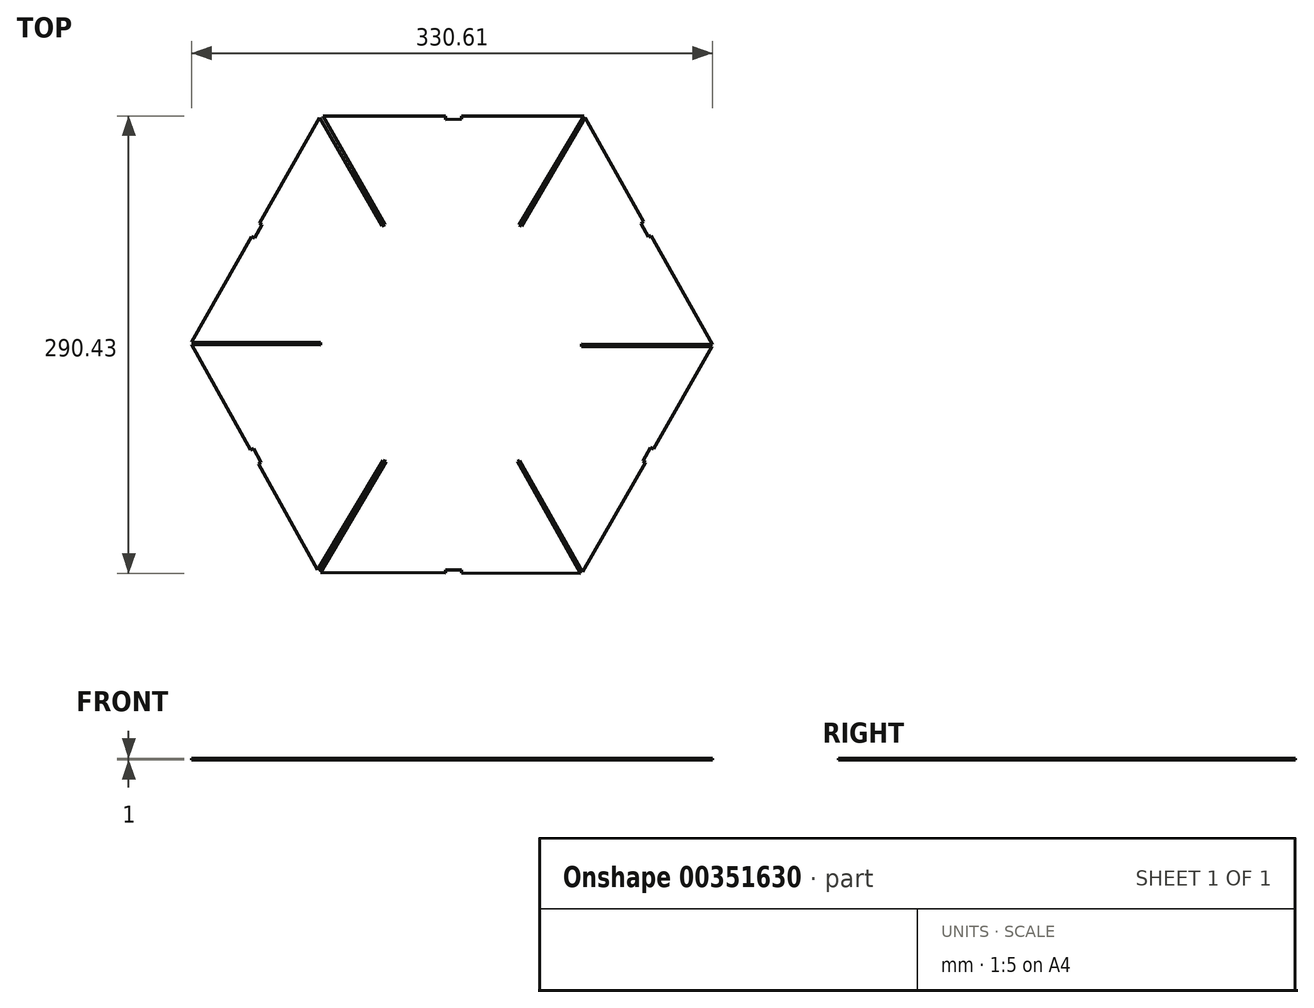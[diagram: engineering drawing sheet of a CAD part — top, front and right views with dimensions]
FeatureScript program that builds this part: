
annotation { "Feature Type Name" : "Feature", "Feature Type Description" : "" }
export const myFeature = defineFeature(function(context is Context, id is Id, definition is map)
    precondition{}
    {
        {
            var Q0;
            Q0=qCreatedBy(makeId("Top.planeOp"),FACE);
            var sketch = newSketch(context, id + "F0", { "sketchPlane" : qUnion([Q0])});
            skLineSegment(sketch, "E0", {"start": v(-250.35, 294.47) * mm, "end": v(-211.1, 225.62) * mm});
            skLineSegment(sketch, "E1", {"start": v(-212.85, 224.65) * mm, "end": v(-252.72, 293.8) * mm});
            skLineSegment(sketch, "E2", {"start": v(-84, 293.57) * mm, "end": v(-124.43, 224.66) * mm});
            skLineSegment(sketch, "E3", {"start": v(-86.95, 4.21) * mm, "end": v(-126.77, 75.2) * mm});
            skLineSegment(sketch, "E4", {"start": v(-126.77, 75.2) * mm, "end": v(-125.57, 76.02) * mm});
            skLineSegment(sketch, "E5", {"start": v(-125.57, 76.02) * mm, "end": v(-85.54, 4.92) * mm});
            skLineSegment(sketch, "E6", {"start": v(-254.03, 6.48) * mm, "end": v(-212.25, 75.92) * mm});
            skLineSegment(sketch, "E7", {"start": v(-252.1, 4.6) * mm, "end": v(-210.48, 75.12) * mm});
            skLineSegment(sketch, "E8", {"start": v(-333.76, 150.95) * mm, "end": v(-252.72, 293.8) * mm});
            skLineSegment(sketch, "E9", {"start": v(-333.76, 149.56) * mm, "end": v(-254.03, 6.48) * mm});
            skLineSegment(sketch, "E10", {"start": v(-252.1, 4.6) * mm, "end": v(-86.95, 4.21) * mm});
            skLineSegment(sketch, "E11", {"start": v(-250.35, 294.47) * mm, "end": v(-84.74, 294.64) * mm});
            skLineSegment(sketch, "E12", {"start": v(-84, 293.57) * mm, "end": v(-3.15, 149.65) * mm});
            skLineSegment(sketch, "E13", {"start": v(112.8, 289.57) * mm, "end": v(239.42, 289.57) * mm});
            skLineSegment(sketch, "E14", {"start": v(240.63, 288.54) * mm, "end": v(303, 178.67) * mm});
            skLineSegment(sketch, "E15", {"start": v(302.98, 177.38) * mm, "end": v(240.54, 67.56) * mm});
            skLineSegment(sketch, "E16", {"start": v(111.35, 67.6) * mm, "end": v(239.28, 67.23) * mm});
            skLineSegment(sketch, "E17", {"start": v(47.38, 177.39) * mm, "end": v(109.98, 67.78) * mm});
            skLineSegment(sketch, "E18", {"start": v(47.44, 178.96) * mm, "end": v(111.62, 289.24) * mm});
            skLineSegment(sketch, "E19", {"start": v(12.87, -130.32) * mm, "end": v(12.87, -166.75) * mm});
            skLineSegment(sketch, "E20", {"start": v(12.87, -166.75) * mm, "end": v(92.46, -167.04) * mm});
            skLineSegment(sketch, "E21", {"start": v(92.46, -167.04) * mm, "end": v(92.46, -168.32) * mm});
            skLineSegment(sketch, "E22", {"start": v(92.46, -168.32) * mm, "end": v(13.17, -168.32) * mm});
            skLineSegment(sketch, "E23", {"start": v(13.17, -168.32) * mm, "end": v(12.87, -198.92) * mm});
            skLineSegment(sketch, "E24", {"start": v(12.87, -198.92) * mm, "end": v(13.17, -205.1) * mm});
            skLineSegment(sketch, "E25", {"start": v(13.17, -205.1) * mm, "end": v(12.87, -235.71) * mm});
            skLineSegment(sketch, "E26", {"start": v(12.87, -235.71) * mm, "end": v(73.4, -236) * mm});
            skLineSegment(sketch, "E27", {"start": v(73.4, -236) * mm, "end": v(73.4, -237.3) * mm});
            skLineSegment(sketch, "E28", {"start": v(73.4, -237.3) * mm, "end": v(13.17, -237.3) * mm});
            skLineSegment(sketch, "E29", {"start": v(13.17, -237.3) * mm, "end": v(12.87, -270.02) * mm});
            skLineSegment(sketch, "E30", {"start": v(12.87, -270.02) * mm, "end": v(49.25, -270.3) * mm});
            skLineSegment(sketch, "E31", {"start": v(49.25, -270.3) * mm, "end": v(49.25, -271.6) * mm});
            skLineSegment(sketch, "E32", {"start": v(49.25, -271.6) * mm, "end": v(13.17, -271.6) * mm});
            skLineSegment(sketch, "E33", {"start": v(13.17, -271.6) * mm, "end": v(12.87, -287.73) * mm});
            skLineSegment(sketch, "E34", {"start": v(12.87, -287.73) * mm, "end": v(21.59, -287.39) * mm});
            skLineSegment(sketch, "E35", {"start": v(21.59, -287.39) * mm, "end": v(35.18, -285.85) * mm});
            skLineSegment(sketch, "E36", {"start": v(35.18, -285.85) * mm, "end": v(48.35, -283.43) * mm});
            skLineSegment(sketch, "E37", {"start": v(48.35, -283.43) * mm, "end": v(60.91, -280.2) * mm});
            skLineSegment(sketch, "E38", {"start": v(60.91, -280.2) * mm, "end": v(72.63, -276.27) * mm});
            skLineSegment(sketch, "E39", {"start": v(72.63, -276.27) * mm, "end": v(83.5, -271.8) * mm});
            skLineSegment(sketch, "E40", {"start": v(83.5, -271.8) * mm, "end": v(93.48, -266.93) * mm});
            skLineSegment(sketch, "E41", {"start": v(12.87, -96) * mm, "end": v(12.87, -130.32) * mm});
            skLineSegment(sketch, "E42", {"start": v(13.17, -66.1) * mm, "end": v(12.87, -96.01) * mm});
            skLineSegment(sketch, "E43", {"start": v(12.87, -27.4) * mm, "end": v(12.87, -63.82) * mm});
            skLineSegment(sketch, "E44", {"start": v(12.87, -63.82) * mm, "end": v(92.46, -64.1) * mm});
            skLineSegment(sketch, "E45", {"start": v(93.48, 34.15) * mm, "end": v(83.5, 39.02) * mm});
            skLineSegment(sketch, "E46", {"start": v(83.5, 39.02) * mm, "end": v(72.63, 43.5) * mm});
            skLineSegment(sketch, "E47", {"start": v(72.63, 43.5) * mm, "end": v(60.91, 47.42) * mm});
            skLineSegment(sketch, "E48", {"start": v(60.91, 47.42) * mm, "end": v(48.35, 50.64) * mm});
            skLineSegment(sketch, "E49", {"start": v(48.35, 50.64) * mm, "end": v(35.17, 53.07) * mm});
            skLineSegment(sketch, "E50", {"start": v(35.17, 53.07) * mm, "end": v(21.59, 54.6) * mm});
            skLineSegment(sketch, "E51", {"start": v(21.59, 54.6) * mm, "end": v(12.87, 54.95) * mm});
            skLineSegment(sketch, "E52", {"start": v(12.87, 54.95) * mm, "end": v(12.87, 38.75) * mm});
            skLineSegment(sketch, "E53", {"start": v(12.87, 38.75) * mm, "end": v(49.25, 38.47) * mm});
            skLineSegment(sketch, "E54", {"start": v(49.25, 38.47) * mm, "end": v(49.25, 37.17) * mm});
            skLineSegment(sketch, "E55", {"start": v(49.25, 37.17) * mm, "end": v(13.17, 37.17) * mm});
            skLineSegment(sketch, "E56", {"start": v(13.17, 37.17) * mm, "end": v(12.87, 5.16) * mm});
            skLineSegment(sketch, "E57", {"start": v(12.87, 5.16) * mm, "end": v(73.39, 4.86) * mm});
            skLineSegment(sketch, "E58", {"start": v(73.39, 4.86) * mm, "end": v(73.39, 3.22) * mm});
            skLineSegment(sketch, "E59", {"start": v(73.39, 3.22) * mm, "end": v(13.17, 3.22) * mm});
            skLineSegment(sketch, "E60", {"start": v(13.17, 3.22) * mm, "end": v(12.87, -27.4) * mm});
            skLineSegment(sketch, "E61", {"start": v(92.1, -168.46) * mm, "end": v(12.87, -168.45) * mm});
            skLineSegment(sketch, "E62", {"start": v(12.87, -168.45) * mm, "end": v(12.87, -166.95) * mm});
            skLineSegment(sketch, "E63", {"start": v(12.87, -166.95) * mm, "end": v(92.1, -166.96) * mm});
            skLineSegment(sketch, "E64", {"start": v(92.1, -166.96) * mm, "end": v(92.1, -168.46) * mm});
            skLineSegment(sketch, "E65", {"start": v(171.06, -171.15) * mm, "end": v(93.48, -266.93) * mm});
            skLineSegment(sketch, "E66", {"start": v(93.48, 34.15) * mm, "end": v(171.18, -62) * mm});
            skLineSegment(sketch, "E67", {"start": v(171.18, -62) * mm, "end": v(171.06, -171.15) * mm});
            skLineSegment(sketch, "E68", {"start": v(92.24, -65.74) * mm, "end": v(13.02, -65.73) * mm});
            skLineSegment(sketch, "E69", {"start": v(13.02, -65.73) * mm, "end": v(13.02, -64.23) * mm});
            skLineSegment(sketch, "E70", {"start": v(13.02, -64.23) * mm, "end": v(92.24, -64.24) * mm});
            skLineSegment(sketch, "E71", {"start": v(92.24, -64.24) * mm, "end": v(92.24, -65.74) * mm});
            skLineSegment(sketch, "E72", {"start": v(12.87, -66) * mm, "end": v(92.46, -66) * mm});
            skLineSegment(sketch, "E73", {"start": v(73.01, 3.26) * mm, "end": v(13.02, 3.27) * mm});
            skLineSegment(sketch, "E74", {"start": v(13.02, 3.27) * mm, "end": v(13.02, 4.77) * mm});
            skLineSegment(sketch, "E75", {"start": v(13.02, 4.77) * mm, "end": v(73.01, 4.76) * mm});
            skLineSegment(sketch, "E76", {"start": v(73.01, 4.76) * mm, "end": v(73.01, 3.26) * mm});
            skLineSegment(sketch, "E77", {"start": v(73.42, -237.43) * mm, "end": v(12.87, -237.42) * mm});
            skLineSegment(sketch, "E78", {"start": v(12.87, -237.42) * mm, "end": v(12.87, -235.92) * mm});
            skLineSegment(sketch, "E79", {"start": v(12.87, -235.92) * mm, "end": v(73.42, -235.93) * mm});
            skLineSegment(sketch, "E80", {"start": v(73.42, -235.93) * mm, "end": v(73.42, -237.43) * mm});
            skLineSegment(sketch, "E81", {"start": v(48.74, -271.47) * mm, "end": v(12.87, -271.46) * mm});
            skLineSegment(sketch, "E82", {"start": v(12.87, -271.46) * mm, "end": v(12.87, -269.96) * mm});
            skLineSegment(sketch, "E83", {"start": v(12.87, -269.96) * mm, "end": v(48.74, -269.97) * mm});
            skLineSegment(sketch, "E84", {"start": v(48.74, -269.97) * mm, "end": v(48.74, -271.47) * mm});
            skLineSegment(sketch, "E85", {"start": v(49.27, 37.27) * mm, "end": v(12.88, 37.28) * mm});
            skLineSegment(sketch, "E86", {"start": v(12.88, 37.28) * mm, "end": v(12.88, 38.78) * mm});
            skLineSegment(sketch, "E87", {"start": v(12.88, 38.78) * mm, "end": v(49.27, 38.77) * mm});
            skLineSegment(sketch, "E88", {"start": v(49.27, 38.77) * mm, "end": v(49.27, 37.27) * mm});
            skLineSegment(sketch, "E89", {"start": v(176.64, -137.23) * mm, "end": v(176.64, -173.66) * mm});
            skLineSegment(sketch, "E90", {"start": v(176.64, -173.66) * mm, "end": v(256.22, -173.94) * mm});
            skLineSegment(sketch, "E91", {"start": v(256.22, -173.94) * mm, "end": v(256.22, -175.22) * mm});
            skLineSegment(sketch, "E92", {"start": v(256.22, -175.22) * mm, "end": v(176.94, -175.22) * mm});
            skLineSegment(sketch, "E93", {"start": v(176.94, -175.22) * mm, "end": v(176.64, -205.83) * mm});
            skLineSegment(sketch, "E94", {"start": v(176.64, -205.83) * mm, "end": v(176.94, -212) * mm});
            skLineSegment(sketch, "E95", {"start": v(176.94, -212) * mm, "end": v(176.64, -242.62) * mm});
            skLineSegment(sketch, "E96", {"start": v(176.64, -242.62) * mm, "end": v(237.16, -242.91) * mm});
            skLineSegment(sketch, "E97", {"start": v(237.16, -242.91) * mm, "end": v(237.16, -244.2) * mm});
            skLineSegment(sketch, "E98", {"start": v(237.16, -244.2) * mm, "end": v(176.94, -244.2) * mm});
            skLineSegment(sketch, "E99", {"start": v(176.94, -244.2) * mm, "end": v(176.64, -276.93) * mm});
            skLineSegment(sketch, "E100", {"start": v(176.64, -276.93) * mm, "end": v(213, -277.22) * mm});
            skLineSegment(sketch, "E101", {"start": v(213, -277.22) * mm, "end": v(213, -278.5) * mm});
            skLineSegment(sketch, "E102", {"start": v(213, -278.5) * mm, "end": v(176.94, -278.5) * mm});
            skLineSegment(sketch, "E103", {"start": v(176.94, -278.5) * mm, "end": v(176.64, -294.64) * mm});
            skLineSegment(sketch, "E104", {"start": v(176.64, -294.64) * mm, "end": v(185.35, -294.3) * mm});
            skLineSegment(sketch, "E105", {"start": v(185.35, -294.3) * mm, "end": v(198.95, -292.76) * mm});
            skLineSegment(sketch, "E106", {"start": v(198.95, -292.76) * mm, "end": v(212.12, -290.34) * mm});
            skLineSegment(sketch, "E107", {"start": v(212.12, -290.34) * mm, "end": v(224.68, -287.1) * mm});
            skLineSegment(sketch, "E108", {"start": v(224.68, -287.1) * mm, "end": v(236.4, -283.18) * mm});
            skLineSegment(sketch, "E109", {"start": v(236.4, -283.18) * mm, "end": v(247.26, -278.72) * mm});
            skLineSegment(sketch, "E110", {"start": v(247.26, -278.72) * mm, "end": v(257.25, -273.84) * mm});
            skLineSegment(sketch, "E111", {"start": v(176.64, -102.91) * mm, "end": v(176.64, -137.23) * mm});
            skLineSegment(sketch, "E112", {"start": v(176.94, -73.02) * mm, "end": v(176.64, -102.92) * mm});
            skLineSegment(sketch, "E113", {"start": v(176.64, -34.3) * mm, "end": v(176.64, -70.73) * mm});
            skLineSegment(sketch, "E114", {"start": v(176.64, -70.73) * mm, "end": v(256.22, -71.02) * mm});
            skLineSegment(sketch, "E115", {"start": v(257.25, 27.24) * mm, "end": v(247.26, 32.11) * mm});
            skLineSegment(sketch, "E116", {"start": v(247.26, 32.11) * mm, "end": v(236.4, 36.6) * mm});
            skLineSegment(sketch, "E117", {"start": v(236.4, 36.6) * mm, "end": v(224.68, 40.51) * mm});
            skLineSegment(sketch, "E118", {"start": v(224.68, 40.51) * mm, "end": v(212.12, 43.73) * mm});
            skLineSegment(sketch, "E119", {"start": v(212.12, 43.73) * mm, "end": v(198.94, 46.16) * mm});
            skLineSegment(sketch, "E120", {"start": v(198.94, 46.16) * mm, "end": v(185.35, 47.7) * mm});
            skLineSegment(sketch, "E121", {"start": v(185.35, 47.7) * mm, "end": v(176.64, 48.04) * mm});
            skLineSegment(sketch, "E122", {"start": v(176.64, 48.04) * mm, "end": v(176.64, 31.84) * mm});
            skLineSegment(sketch, "E123", {"start": v(176.64, 31.84) * mm, "end": v(213, 31.56) * mm});
            skLineSegment(sketch, "E124", {"start": v(213, 31.56) * mm, "end": v(213, 30.27) * mm});
            skLineSegment(sketch, "E125", {"start": v(213, 30.27) * mm, "end": v(176.94, 30.27) * mm});
            skLineSegment(sketch, "E126", {"start": v(176.94, 30.27) * mm, "end": v(176.64, -1.75) * mm});
            skLineSegment(sketch, "E127", {"start": v(176.64, -1.75) * mm, "end": v(237.15, -2.05) * mm});
            skLineSegment(sketch, "E128", {"start": v(237.15, -2.05) * mm, "end": v(237.15, -3.69) * mm});
            skLineSegment(sketch, "E129", {"start": v(237.15, -3.69) * mm, "end": v(176.94, -3.69) * mm});
            skLineSegment(sketch, "E130", {"start": v(176.94, -3.69) * mm, "end": v(176.64, -34.3) * mm});
            skLineSegment(sketch, "E131", {"start": v(255.85, -175.37) * mm, "end": v(176.64, -175.36) * mm});
            skLineSegment(sketch, "E132", {"start": v(176.64, -175.36) * mm, "end": v(176.64, -173.86) * mm});
            skLineSegment(sketch, "E133", {"start": v(176.64, -173.86) * mm, "end": v(255.85, -173.87) * mm});
            skLineSegment(sketch, "E134", {"start": v(255.85, -173.87) * mm, "end": v(255.85, -175.37) * mm});
            skLineSegment(sketch, "E135", {"start": v(334.82, -178.06) * mm, "end": v(257.25, -273.84) * mm});
            skLineSegment(sketch, "E136", {"start": v(257.25, 27.24) * mm, "end": v(334.94, -68.92) * mm});
            skLineSegment(sketch, "E137", {"start": v(334.94, -68.92) * mm, "end": v(334.82, -178.06) * mm});
            skLineSegment(sketch, "E138", {"start": v(256, -72.65) * mm, "end": v(176.79, -72.63) * mm});
            skLineSegment(sketch, "E139", {"start": v(176.79, -72.63) * mm, "end": v(176.79, -71.13) * mm});
            skLineSegment(sketch, "E140", {"start": v(176.79, -71.13) * mm, "end": v(256, -71.15) * mm});
            skLineSegment(sketch, "E141", {"start": v(256, -71.15) * mm, "end": v(256, -72.65) * mm});
            skLineSegment(sketch, "E142", {"start": v(176.64, -72.91) * mm, "end": v(256.22, -72.91) * mm});
            skLineSegment(sketch, "E143", {"start": v(236.78, -3.65) * mm, "end": v(176.79, -3.64) * mm});
            skLineSegment(sketch, "E144", {"start": v(176.79, -3.64) * mm, "end": v(176.79, -2.14) * mm});
            skLineSegment(sketch, "E145", {"start": v(176.79, -2.14) * mm, "end": v(236.78, -2.15) * mm});
            skLineSegment(sketch, "E146", {"start": v(236.78, -2.15) * mm, "end": v(236.78, -3.65) * mm});
            skLineSegment(sketch, "E147", {"start": v(237.19, -244.34) * mm, "end": v(176.64, -244.32) * mm});
            skLineSegment(sketch, "E148", {"start": v(176.64, -244.32) * mm, "end": v(176.64, -242.82) * mm});
            skLineSegment(sketch, "E149", {"start": v(176.64, -242.82) * mm, "end": v(237.19, -242.84) * mm});
            skLineSegment(sketch, "E150", {"start": v(237.19, -242.84) * mm, "end": v(237.19, -244.34) * mm});
            skLineSegment(sketch, "E151", {"start": v(212.5, -278.38) * mm, "end": v(176.64, -278.37) * mm});
            skLineSegment(sketch, "E152", {"start": v(176.64, -278.37) * mm, "end": v(176.64, -276.87) * mm});
            skLineSegment(sketch, "E153", {"start": v(176.64, -276.87) * mm, "end": v(212.5, -276.88) * mm});
            skLineSegment(sketch, "E154", {"start": v(212.5, -276.88) * mm, "end": v(212.5, -278.38) * mm});
            skLineSegment(sketch, "E155", {"start": v(213.04, 30.36) * mm, "end": v(176.65, 30.37) * mm});
            skLineSegment(sketch, "E156", {"start": v(176.65, 30.37) * mm, "end": v(176.65, 31.87) * mm});
            skLineSegment(sketch, "E157", {"start": v(176.65, 31.87) * mm, "end": v(213.04, 31.86) * mm});
            skLineSegment(sketch, "E158", {"start": v(213.04, 31.86) * mm, "end": v(213.04, 30.36) * mm});
            skLineSegment(sketch, "E159", {"start": v(-84.74, 294.64) * mm, "end": v(-125.8, 225.5) * mm});
            skLineSegment(sketch, "E160", {"start": v(-251.86, 149.23) * mm, "end": v(-333.76, 149.56) * mm});
            skLineSegment(sketch, "E161", {"start": v(-333.76, 150.96) * mm, "end": v(-333.76, 150.96) * mm});
            skLineSegment(sketch, "E162", {"start": v(-333.76, 150.96) * mm, "end": v(-251.85, 150.64) * mm});
            skLineSegment(sketch, "E163", {"start": v(-86.22, 149.98) * mm, "end": v(-3.15, 149.65) * mm});
            skLineSegment(sketch, "E164", {"start": v(-3.32, 148.25) * mm, "end": v(-86.27, 148.22) * mm});
            skLineSegment(sketch, "E165", {"start": v(47.87, 179.02) * mm, "end": v(109.23, 178.78) * mm});
            skLineSegment(sketch, "E166", {"start": v(109.23, 178.78) * mm, "end": v(109.22, 177.38) * mm});
            skLineSegment(sketch, "E167", {"start": v(109.22, 177.38) * mm, "end": v(47.35, 177.62) * mm});
            skLineSegment(sketch, "E168", {"start": v(241.63, 179.02) * mm, "end": v(302.98, 178.78) * mm});
            skLineSegment(sketch, "E169", {"start": v(302.98, 178.78) * mm, "end": v(302.98, 177.38) * mm});
            skLineSegment(sketch, "E170", {"start": v(302.98, 177.38) * mm, "end": v(241.63, 177.62) * mm});
            skLineSegment(sketch, "E171", {"start": v(-251.85, 150.64) * mm, "end": v(-251.86, 149.23) * mm});
            skLineSegment(sketch, "E172", {"start": v(-86.22, 149.98) * mm, "end": v(-86.27, 148.22) * mm});
            skLineSegment(sketch, "E173", {"start": v(-248.6, -2.14) * mm, "end": v(-252.57, -2.14) * mm});
            skLineSegment(sketch, "E174", {"start": v(-252.57, -2.14) * mm, "end": v(-212.18, -72.78) * mm});
            skLineSegment(sketch, "E175", {"start": v(-212.18, -72.78) * mm, "end": v(-213.4, -73.24) * mm});
            skLineSegment(sketch, "E176", {"start": v(-213.4, -73.24) * mm, "end": v(-253.9, -2.98) * mm});
            skLineSegment(sketch, "E177", {"start": v(-85.17, -3.2) * mm, "end": v(-126.38, -73.58) * mm});
            skLineSegment(sketch, "E178", {"start": v(-126.38, -73.58) * mm, "end": v(-127.79, -72.55) * mm});
            skLineSegment(sketch, "E179", {"start": v(-88.13, -292.57) * mm, "end": v(-127.95, -221.58) * mm});
            skLineSegment(sketch, "E180", {"start": v(-127.95, -221.58) * mm, "end": v(-126.75, -220.77) * mm});
            skLineSegment(sketch, "E181", {"start": v(-126.75, -220.77) * mm, "end": v(-86.72, -291.87) * mm});
            skLineSegment(sketch, "E182", {"start": v(-254.23, -290.57) * mm, "end": v(-213.04, -220.78) * mm});
            skLineSegment(sketch, "E183", {"start": v(-213.04, -220.78) * mm, "end": v(-211.67, -221.79) * mm});
            skLineSegment(sketch, "E184", {"start": v(-253.27, -292.2) * mm, "end": v(-211.67, -221.66) * mm});
            skLineSegment(sketch, "E185", {"start": v(-334.94, -145.83) * mm, "end": v(-253.9, -2.98) * mm});
            skLineSegment(sketch, "E186", {"start": v(-334.94, -147.23) * mm, "end": v(-254.23, -290.57) * mm});
            skLineSegment(sketch, "E187", {"start": v(-253.27, -292.2) * mm, "end": v(-88.36, -292.54) * mm});
            skLineSegment(sketch, "E188", {"start": v(-86.72, -291.87) * mm, "end": v(-4.33, -148.76) * mm});
            skLineSegment(sketch, "E189", {"start": v(-249.9, -2.14) * mm, "end": v(-85.92, -2.14) * mm});
            skLineSegment(sketch, "E190", {"start": v(-85.17, -3.2) * mm, "end": v(-4.33, -147.26) * mm});
            skLineSegment(sketch, "E191", {"start": v(-213.34, -73.46) * mm, "end": v(-214.08, -72.16) * mm});
            skLineSegment(sketch, "E192", {"start": v(-214.08, -72.16) * mm, "end": v(-212.77, -71.42) * mm});
            skLineSegment(sketch, "E193", {"start": v(-212.77, -71.42) * mm, "end": v(-212.03, -72.73) * mm});
            skLineSegment(sketch, "E194", {"start": v(-212.03, -72.73) * mm, "end": v(-213.34, -73.46) * mm});
            skLineSegment(sketch, "E195", {"start": v(-126.52, -73.36) * mm, "end": v(-127.79, -72.55) * mm});
            skLineSegment(sketch, "E196", {"start": v(-127.79, -72.55) * mm, "end": v(-126.98, -71.29) * mm});
            skLineSegment(sketch, "E197", {"start": v(-126.98, -71.29) * mm, "end": v(-125.71, -72.1) * mm});
            skLineSegment(sketch, "E198", {"start": v(-125.71, -72.1) * mm, "end": v(-126.52, -73.36) * mm});
            skLineSegment(sketch, "E199", {"start": v(-85.92, -2.14) * mm, "end": v(-127.79, -72.55) * mm});
            skLineSegment(sketch, "E200", {"start": v(-253.04, -147.55) * mm, "end": v(-334.94, -147.23) * mm});
            skLineSegment(sketch, "E201", {"start": v(-334.94, -147.23) * mm, "end": v(-334.94, -145.82) * mm});
            skLineSegment(sketch, "E202", {"start": v(-334.94, -145.82) * mm, "end": v(-253.04, -146.15) * mm});
            skLineSegment(sketch, "E203", {"start": v(-87.23, -146.8) * mm, "end": v(-4.33, -147.13) * mm});
            skLineSegment(sketch, "E204", {"start": v(-4.33, -147.13) * mm, "end": v(-4.33, -148.53) * mm});
            skLineSegment(sketch, "E205", {"start": v(-4.33, -148.53) * mm, "end": v(-87.47, -148.2) * mm});
            skLineSegment(sketch, "E206", {"start": v(-253.04, -146.15) * mm, "end": v(-253.04, -147.55) * mm});
            skLineSegment(sketch, "E207", {"start": v(-87.23, -146.8) * mm, "end": v(-87.47, -148.2) * mm});
            skLineSegment(sketch, "E208", {"start": v(241.63, 179.02) * mm, "end": v(241.63, 177.62) * mm});
            skLineSegment(sketch, "E209", {"start": v(208.5, 236.25) * mm, "end": v(239.42, 289.24) * mm});
            skLineSegment(sketch, "E210", {"start": v(239.42, 289.24) * mm, "end": v(240.63, 288.54) * mm});
            skLineSegment(sketch, "E211", {"start": v(240.63, 288.54) * mm, "end": v(209.44, 235.1) * mm});
            skLineSegment(sketch, "E212", {"start": v(109.98, 67.78) * mm, "end": v(141.33, 121.75) * mm});
            skLineSegment(sketch, "E213", {"start": v(141.33, 121.75) * mm, "end": v(142.54, 121.04) * mm});
            skLineSegment(sketch, "E214", {"start": v(142.54, 121.04) * mm, "end": v(111.35, 67.6) * mm});
            skLineSegment(sketch, "E215", {"start": v(240.5, 67.6) * mm, "end": v(207.83, 121.05) * mm});
            skLineSegment(sketch, "E216", {"start": v(207.83, 121.05) * mm, "end": v(207.02, 119.77) * mm});
            skLineSegment(sketch, "E217", {"start": v(207.02, 119.77) * mm, "end": v(239.4, 67.04) * mm});
            skLineSegment(sketch, "E218", {"start": v(143.5, 235.92) * mm, "end": v(112.45, 290.33) * mm});
            skLineSegment(sketch, "E219", {"start": v(112.45, 290.33) * mm, "end": v(111.6, 289.08) * mm});
            skLineSegment(sketch, "E220", {"start": v(111.6, 289.08) * mm, "end": v(142.37, 235.4) * mm});
            skLineSegment(sketch, "E221", {"start": v(142.37, 235.4) * mm, "end": v(143.5, 235.92) * mm});
            skLineSegment(sketch, "E222", {"start": v(208.5, 236.25) * mm, "end": v(209.44, 235.1) * mm});
            skLineSegment(sketch, "E223", {"start": v(-212.85, 224.65) * mm, "end": v(-211.1, 225.62) * mm});
            skLineSegment(sketch, "E224", {"start": v(-3.32, 148.25) * mm, "end": v(-85.54, 4.92) * mm});
            skLineSegment(sketch, "E225", {"start": v(-125.8, 225.5) * mm, "end": v(-124.43, 224.66) * mm});
            skLineSegment(sketch, "E226", {"start": v(-212.25, 75.92) * mm, "end": v(-210.48, 75.12) * mm});
            skSolve(sketch);
        }
        {
            var Q0;
            Q0=makeQuery(id+"F0.imprint","IMPRINT",FACE,{"disambiguationData":[TD([[makeQuery(id+"F0.imprint","IMPRINT",EDGE,{"derivedFrom":sQuery(id+"F0.wireOp",EDGE,"E0")}),1.0]])]});
            extrude(context, id + "F1", {"entities" : qUnion([Q0]), "depth" : 1 * mm});
        }
        {
            var Q0;
            Q0=makeQuery(id+"F1.opExtrude","CAP_FACE",FACE,{"disambiguationData":[OSD([sQuery(id+"F0.wireOp",EDGE,"E0"),sQuery(id+"F0.wireOp",EDGE,"E1"),sQuery(id+"F0.wireOp",EDGE,"E2"),sQuery(id+"F0.wireOp",EDGE,"E3"),sQuery(id+"F0.wireOp",EDGE,"E4"),sQuery(id+"F0.wireOp",EDGE,"E5"),sQuery(id+"F0.wireOp",EDGE,"E6"),sQuery(id+"F0.wireOp",EDGE,"E7"),sQuery(id+"F0.wireOp",EDGE,"E8"),sQuery(id+"F0.wireOp",EDGE,"E9"),sQuery(id+"F0.wireOp",EDGE,"E10"),sQuery(id+"F0.wireOp",EDGE,"E11"),sQuery(id+"F0.wireOp",EDGE,"E12"),sQuery(id+"F0.wireOp",EDGE,"E159"),sQuery(id+"F0.wireOp",EDGE,"E160"),sQuery(id+"F0.wireOp",EDGE,"E162"),sQuery(id+"F0.wireOp",EDGE,"E163"),sQuery(id+"F0.wireOp",EDGE,"E164"),sQuery(id+"F0.wireOp",EDGE,"E171"),sQuery(id+"F0.wireOp",EDGE,"E172"),sQuery(id+"F0.wireOp",EDGE,"E223"),sQuery(id+"F0.wireOp",EDGE,"E224"),sQuery(id+"F0.wireOp",EDGE,"E225"),sQuery(id+"F0.wireOp",EDGE,"E226")])],"isStart":false});
            var sketch = newSketch(context, id + "F2", { "sketchPlane" : qUnion([Q0])});
            skLineSegment(sketch, "E227.0", {"start": v(-172.55, 6.4) * mm, "end": v(-162.55, 6.38) * mm, "construction": true});
            skLineSegment(sketch, "E228.bottom", {"start": v(-172.55, 4.4) * mm, "end": v(-162.55, 4.4) * mm});
            skLineSegment(sketch, "E228.top", {"start": v(-172.55, 6.38) * mm, "end": v(-162.55, 6.38) * mm});
            skLineSegment(sketch, "E228.left", {"start": v(-172.55, 4.4) * mm, "end": v(-172.55, 6.38) * mm});
            skLineSegment(sketch, "E228.right", {"start": v(-162.55, 4.4) * mm, "end": v(-162.55, 6.38) * mm});
            skLineSegment(sketch, "E229.0", {"start": v(-250.35, 292.47) * mm, "end": v(-84.74, 292.64) * mm, "construction": true});
            skLineSegment(sketch, "E230", {"start": v(-172.55, 294.56) * mm, "end": v(-172.55, 292.55) * mm});
            skLineSegment(sketch, "E231", {"start": v(-172.55, 292.55) * mm, "end": v(-162.55, 292.56) * mm});
            skPoint(sketch, "E231.endSnap0", {"position": v(-167.55, 292.56) * mm});
            skLineSegment(sketch, "E232", {"start": v(-162.55, 292.56) * mm, "end": v(-162.55, 294.56) * mm});
            skLineSegment(sketch, "E233", {"start": v(-162.55, 294.56) * mm, "end": v(-172.55, 294.56) * mm});
            skPoint(sketch, "E234.endSnap0", {"position": v(-44.43, 76.59) * mm});
            skLineSegment(sketch, "E235.0", {"start": v(-332.02, 149.97) * mm, "end": v(-250.98, 292.82) * mm, "construction": true});
            skLineSegment(sketch, "E236.0", {"start": v(-85.74, 292.6) * mm, "end": v(-4.89, 148.67) * mm, "construction": true});
            skLineSegment(sketch, "E237.0", {"start": v(-332.01, 150.53) * mm, "end": v(-331.86, 150.25) * mm, "construction": true});
            skLineSegment(sketch, "E238", {"start": v(-46.94, 227.46) * mm, "end": v(-41.91, 218.82) * mm});
            skLineSegment(sketch, "E239", {"start": v(-41.91, 218.82) * mm, "end": v(-43.7, 217.78) * mm});
            skLineSegment(sketch, "E240", {"start": v(-43.7, 217.78) * mm, "end": v(-48.6, 226.5) * mm});
            skLineSegment(sketch, "E241", {"start": v(-48.6, 226.5) * mm, "end": v(-46.94, 227.46) * mm});
            skLineSegment(sketch, "E242", {"start": v(-295.72, 218.04) * mm, "end": v(-290.75, 226.72) * mm});
            skLineSegment(sketch, "E243", {"start": v(-290.75, 226.72) * mm, "end": v(-289.03, 225.74) * mm});
            skLineSegment(sketch, "E244", {"start": v(-289.03, 225.74) * mm, "end": v(-293.97, 217.04) * mm});
            skLineSegment(sketch, "E245", {"start": v(-293.97, 217.04) * mm, "end": v(-295.72, 218.04) * mm});
            skLineSegment(sketch, "E246", {"start": v(-296.4, 82.34) * mm, "end": v(-294.58, 83.36) * mm});
            skLineSegment(sketch, "E247", {"start": v(-291.38, 73.7) * mm, "end": v(-289.73, 74.66) * mm});
            skLineSegment(sketch, "E248", {"start": v(-289.73, 74.66) * mm, "end": v(-294.58, 83.36) * mm});
            skLineSegment(sketch, "E249", {"start": v(-296.4, 82.34) * mm, "end": v(-291.38, 73.7) * mm});
            skLineSegment(sketch, "E250.trimOffspring", {"start": v(-294.6, 83.4) * mm, "end": v(-296.4, 82.34) * mm, "construction": true});
            skLineSegment(sketch, "E251.trimOffspring", {"start": v(-292.17, 79.03) * mm, "end": v(-293.9, 78.02) * mm, "construction": true});
            skLineSegment(sketch, "E252.trimOffspring", {"start": v(-289.73, 74.66) * mm, "end": v(-291.38, 73.7) * mm, "construction": true});
            skLineSegment(sketch, "E253.trimOffspring", {"start": v(-294.6, 83.4) * mm, "end": v(-289.73, 74.66) * mm, "construction": true});
            skLineSegment(sketch, "E254", {"start": v(-47.32, 75.56) * mm, "end": v(-45.59, 74.56) * mm});
            skLineSegment(sketch, "E255", {"start": v(-47.32, 75.56) * mm, "end": v(-42.35, 84.23) * mm});
            skLineSegment(sketch, "E256", {"start": v(-42.35, 84.23) * mm, "end": v(-40.61, 83.24) * mm});
            skLineSegment(sketch, "E257", {"start": v(-45.59, 74.56) * mm, "end": v(-40.61, 83.24) * mm});
            skLineSegment(sketch, "E258.trimOffspring", {"start": v(-44.83, 79.9) * mm, "end": v(-44.43, 79.66) * mm, "construction": true});
            skLineSegment(sketch, "E259.trimOffspring", {"start": v(-42.35, 84.23) * mm, "end": v(-41.94, 84) * mm, "construction": true});
            skSolve(sketch);
        }
        {
            var Q0;
            {var subQ2=sQuery(id+"F2.wireOp",EDGE,"E228.top");Q0=makeQuery(id+"F2.imprint","IMPRINT",FACE,{"disambiguationData":[TD([[makeQuery(id+"F2.imprint","IMPRINT",EDGE,{"derivedFrom":subQ2}),-1.0]])]});}
            extrude(context, id + "F3", {"entities" : qUnion([Q0]), "operationType" : NewBodyOperationType.REMOVE, "oppositeDirection" : true, "depth" : 1 * mm});
        }
        {
            var Q0;
            {var subQ13=sQuery(id+"F0.wireOp",EDGE,"E10");var subQ20=sQuery(id+"F0.wireOp",EDGE,"E3");Q0=makeQuery(id+"F3.boolean.opBoolean","SPLIT",FACE,{"disambiguationData":[TD([makeQuery(id+"F1.opExtrude","SWEPT_FACE",FACE,{"disambiguationData":[OSD([subQ20])]})])],"derivedFrom":makeQuery(id+"F1.opExtrude","SWEPT_FACE",FACE,{"disambiguationData":[OSD([subQ13])]})});}
            var sketch = newSketch(context, id + "F4", { "sketchPlane" : qUnion([Q0])});
            skLineSegment(sketch, "E260.bottom", {"start": v(-162.56, 1) * mm, "end": v(-167.56, 1) * mm});
            skLineSegment(sketch, "E260.top", {"start": v(-162.56, 0) * mm, "end": v(-167.56, 0) * mm});
            skLineSegment(sketch, "E260.left", {"start": v(-162.56, 1) * mm, "end": v(-162.56, 0) * mm});
            skLineSegment(sketch, "E260.right", {"start": v(-167.56, 1) * mm, "end": v(-167.56, 0) * mm});
            skSolve(sketch);
        }
        {
            var Q0;
            Q0=makeQuery(id+"F4.imprint","IMPRINT",FACE,{"disambiguationData":[TD([[makeQuery(id+"F4.imprint","IMPRINT",EDGE,{"derivedFrom":sQuery(id+"F4.wireOp",EDGE,"E260.bottom")}),-1.0]])]});
            extrude(context, id + "F5", {"entities" : qUnion([Q0]), "operationType" : NewBodyOperationType.REMOVE, "oppositeDirection" : true, "depth" : 0.5 * mm});
        }
        {
            var Q0;
            {var subQ1=sQuery(id+"F2.wireOp",EDGE,"E247");Q0=makeQuery(id+"F2.imprint","IMPRINT",FACE,{"disambiguationData":[TD([[makeQuery(id+"F2.imprint","IMPRINT",EDGE,{"derivedFrom":subQ1}),1.0]])]});}
            var Q1;
            Q1=makeQuery(id+"F2.imprint","IMPRINT",FACE,{"disambiguationData":[TD([[makeQuery(id+"F2.imprint","IMPRINT",EDGE,{"derivedFrom":sQuery(id+"F2.wireOp",EDGE,"E254")}),1.0]])]});
            var Q2;
            {var subQ0=sQuery(id+"F2.wireOp",EDGE,"E240");Q2=makeQuery(id+"F2.imprint","IMPRINT",FACE,{"disambiguationData":[TD([[makeQuery(id+"F2.imprint","IMPRINT",EDGE,{"derivedFrom":subQ0}),-1.0]])]});}
            var Q3;
            {var subQ4=sQuery(id+"F2.wireOp",EDGE,"E231");Q3=makeQuery(id+"F2.imprint","IMPRINT",FACE,{"disambiguationData":[TD([[makeQuery(id+"F2.imprint","IMPRINT",EDGE,{"derivedFrom":subQ4}),1.0]])]});}
            var Q4;
            {var subQ6=sQuery(id+"F2.wireOp",EDGE,"E243");Q4=makeQuery(id+"F2.imprint","IMPRINT",FACE,{"disambiguationData":[TD([[makeQuery(id+"F2.imprint","IMPRINT",EDGE,{"derivedFrom":subQ6}),-1.0]])]});}
            extrude(context, id + "F6", {"entities" : qUnion([Q0, Q1, Q2, Q3, Q4]), "operationType" : NewBodyOperationType.REMOVE, "oppositeDirection" : true, "depth" : 1.5 * mm});
        }
        {
            var Q0;
            {var subQ14=sQuery(id+"F0.wireOp",EDGE,"E9");var subQ17=sQuery(id+"F0.wireOp",EDGE,"E6");Q0=makeQuery(id+"F6.boolean.opBoolean","SPLIT",FACE,{"disambiguationData":[TD([makeQuery(id+"F1.opExtrude","SWEPT_FACE",FACE,{"disambiguationData":[OSD([subQ17])]})])],"derivedFrom":makeQuery(id+"F1.opExtrude","SWEPT_FACE",FACE,{"disambiguationData":[OSD([subQ14])]})});}
            var sketch = newSketch(context, id + "F7", { "sketchPlane" : qUnion([Q0])});
            skLineSegment(sketch, "E261.bottom", {"start": v(-211.22, 0) * mm, "end": v(-206.21, 0) * mm});
            skLineSegment(sketch, "E261.top", {"start": v(-211.22, 1) * mm, "end": v(-206.21, 1) * mm});
            skLineSegment(sketch, "E261.left", {"start": v(-211.22, 0) * mm, "end": v(-211.22, 1) * mm});
            skLineSegment(sketch, "E261.right", {"start": v(-206.21, 0) * mm, "end": v(-206.21, 1) * mm});
            skSolve(sketch);
        }
        {
            var Q0;
            Q0 = qSketchRegion(id + "F7", true);
            extrude(context, id + "F8", {"entities" : qUnion([Q0]), "operationType" : NewBodyOperationType.REMOVE, "oppositeDirection" : true, "depth" : 0.5 * mm});
        }
        {
            var Q0;
            {var subQ15=sQuery(id+"F0.wireOp",EDGE,"E8");var subQ22=sQuery(id+"F0.wireOp",EDGE,"E1");Q0=makeQuery(id+"F6.boolean.opBoolean","SPLIT",FACE,{"disambiguationData":[TD([makeQuery(id+"F1.opExtrude","SWEPT_FACE",FACE,{"disambiguationData":[OSD([subQ22])]})])],"derivedFrom":makeQuery(id+"F1.opExtrude","SWEPT_FACE",FACE,{"disambiguationData":[OSD([subQ15])]})});}
            var sketch = newSketch(context, id + "F9", { "sketchPlane" : qUnion([Q0])});
            skLineSegment(sketch, "E262.bottom", {"start": v(-48.73, 1) * mm, "end": v(-53.73, 1) * mm});
            skLineSegment(sketch, "E262.top", {"start": v(-48.73, 0) * mm, "end": v(-53.73, 0) * mm});
            skLineSegment(sketch, "E262.left", {"start": v(-48.73, 1) * mm, "end": v(-48.73, 0) * mm});
            skLineSegment(sketch, "E262.right", {"start": v(-53.73, 1) * mm, "end": v(-53.73, 0) * mm});
            skSolve(sketch);
        }
        {
            var Q0;
            Q0 = qSketchRegion(id + "F9", true);
            extrude(context, id + "F10", {"entities" : qUnion([Q0]), "operationType" : NewBodyOperationType.REMOVE, "oppositeDirection" : true, "depth" : 0.5 * mm});
        }
        {
            var Q0;
            {var subQ11=sQuery(id+"F0.wireOp",EDGE,"E12");var subQ21=sQuery(id+"F0.wireOp",EDGE,"E2");Q0=makeQuery(id+"F6.boolean.opBoolean","SPLIT",FACE,{"disambiguationData":[TD([makeQuery(id+"F1.opExtrude","SWEPT_FACE",FACE,{"disambiguationData":[OSD([subQ21])]})])],"derivedFrom":makeQuery(id+"F1.opExtrude","SWEPT_FACE",FACE,{"disambiguationData":[OSD([subQ11])]})});}
            var sketch = newSketch(context, id + "F11", { "sketchPlane" : qUnion([Q0])});
            skLineSegment(sketch, "E263.bottom", {"start": v(221.31, 1) * mm, "end": v(216.3, 1) * mm});
            skLineSegment(sketch, "E263.top", {"start": v(221.31, 0) * mm, "end": v(216.3, 0) * mm});
            skLineSegment(sketch, "E263.left", {"start": v(221.31, 1) * mm, "end": v(221.31, 0) * mm});
            skLineSegment(sketch, "E263.right", {"start": v(216.3, 1) * mm, "end": v(216.3, 0) * mm});
            skSolve(sketch);
        }
        {
            var Q0;
            Q0 = qSketchRegion(id + "F11", true);
            extrude(context, id + "F12", {"entities" : qUnion([Q0]), "operationType" : NewBodyOperationType.REMOVE, "oppositeDirection" : true, "depth" : 0.5 * mm});
        }
    });
